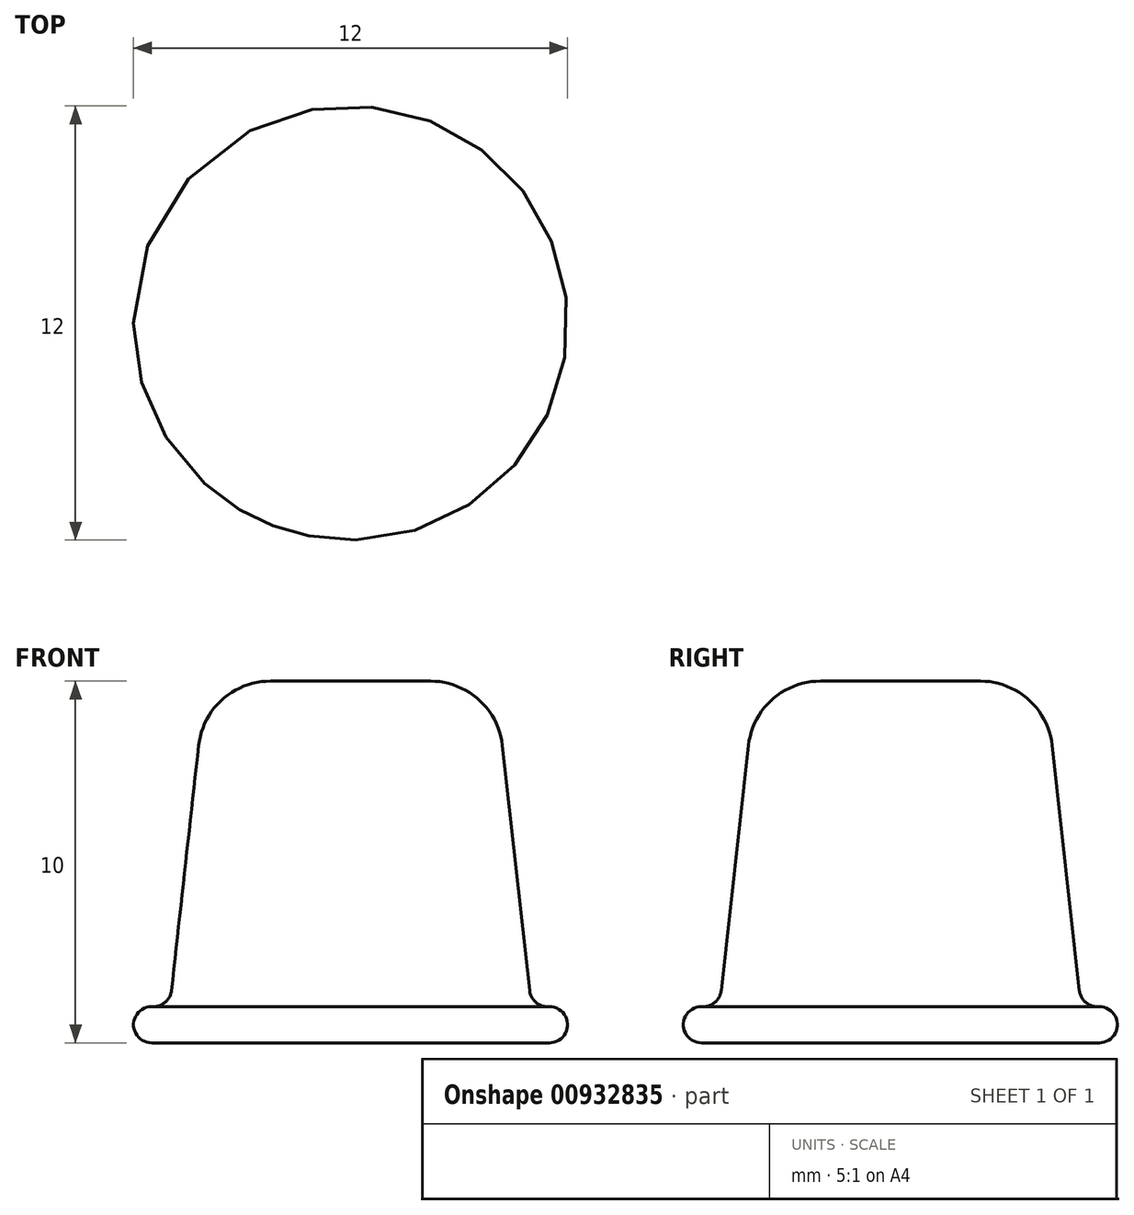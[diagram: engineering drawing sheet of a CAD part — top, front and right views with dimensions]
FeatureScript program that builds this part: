
annotation { "Feature Type Name" : "Feature", "Feature Type Description" : "" }
export const myFeature = defineFeature(function(context is Context, id is Id, definition is map)
    precondition{}
    {
        {
            var Q0;
            Q0=qCreatedBy(makeId("Front.planeOp"),FACE);
            var sketch = newSketch(context, id + "F0", { "sketchPlane" : qUnion([Q0])});
            skLineSegment(sketch, "E0", {"start": v(0, 0) * mm, "end": v(5.5, 0) * mm});
            skLineSegment(sketch, "E1", {"start": v(6, 0.5) * mm, "end": v(6, 0.5) * mm});
            skLineSegment(sketch, "E2", {"start": v(5.5, 1) * mm, "end": v(5, 1) * mm});
            skLineSegment(sketch, "E3", {"start": v(5, 1) * mm, "end": v(4.2, 8.22) * mm});
            skLineSegment(sketch, "E4", {"start": v(2.2, 10) * mm, "end": v(0, 10) * mm});
            skPoint(sketch, "E5.visualSharp", {"position": v(4, 10) * mm});
            skArc(sketch, "E5.filletArc", {"start": v(4.2, 8.22) * mm, "mid": v(3.54, 9.5) * mm, "end": v(2.2, 10) * mm});
            skPoint(sketch, "E6.visualSharp", {"position": v(6, 1) * mm});
            skArc(sketch, "E6.filletArc", {"start": v(6, 0.5) * mm, "mid": v(5.85, 0.85) * mm, "end": v(5.5, 1) * mm});
            skPoint(sketch, "E7.visualSharp", {"position": v(6, 0) * mm});
            skArc(sketch, "E7.filletArc", {"start": v(5.5, 0) * mm, "mid": v(5.85, 0.15) * mm, "end": v(6, 0.5) * mm});
            skLineSegment(sketch, "E8", {"start": v(0, 13.14) * mm, "end": v(0, -7.45) * mm, "construction": true});
            skSolve(sketch);
        }
        {
            var Q0;
            Q0 = qConstructionFilter(qBodyType(qCreatedBy(id + "F0" ,EDGE), BodyType.WIRE), ConstructionObject.NO);
            var Q1;
            Q1=sQuery(id+"F0.wireOp",EDGE,"E8");
            revolve(context, id + "F1", {"bodyType" : ToolBodyType.SURFACE, "surfaceOperationType" : NewSurfaceOperationType.NEW, "surfaceEntities" : qUnion([Q0]), "axis" : qUnion([Q1]), "revolveType" : RevolveType.FULL});
        }
        {
            var Q0;
            Q0=makeQuery(id+"F1.opRevolve","SWEPT_EDGE",EDGE,{"disambiguationData":[OSD([sQuery(id+"F0.wireOp",VERTEX,"E3.start")])]});
            fillet(context, id + "F2", {"entities" : qUnion([Q0]), "radius" : 0.5 * mm, "tangentPropagation" : true, "allowEdgeOverflow" : false});
        }
    });
